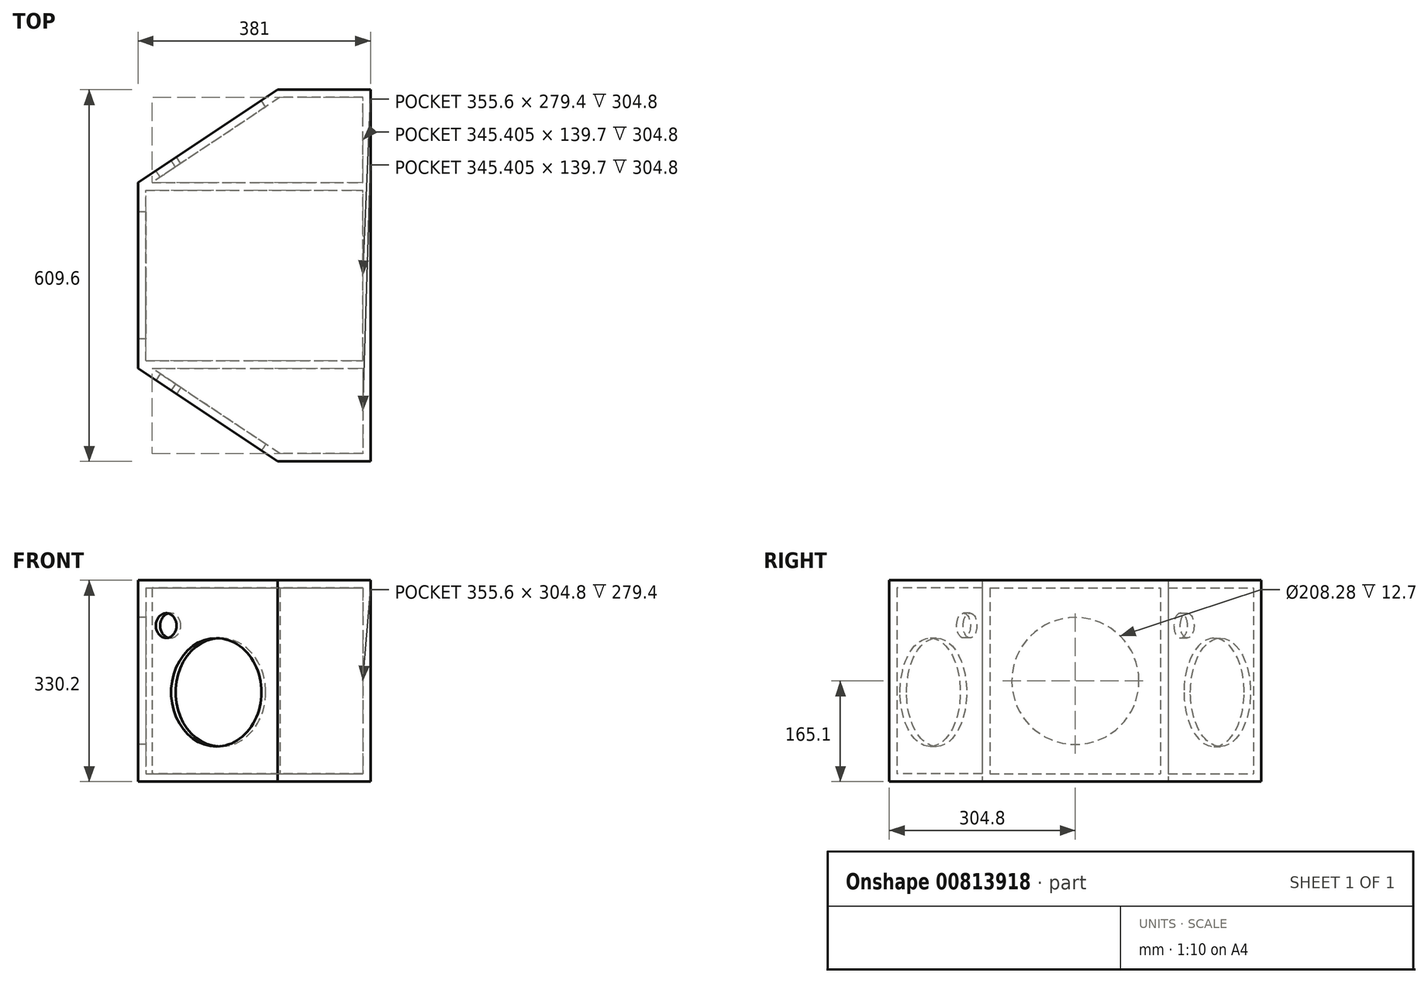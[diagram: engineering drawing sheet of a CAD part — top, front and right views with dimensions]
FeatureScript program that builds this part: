
annotation { "Feature Type Name" : "Feature", "Feature Type Description" : "" }
export const myFeature = defineFeature(function(context is Context, id is Id, definition is map)
    precondition{}
    {
        {
            var Q0;
            Q0=qCreatedBy(makeId("Top.planeOp"),FACE);
            var sketch = newSketch(context, id + "F0", { "sketchPlane" : qUnion([Q0])});
            skLineSegment(sketch, "E0.bottom", {"start": v(0, 0) * mm, "end": v(381, 0) * mm});
            skLineSegment(sketch, "E0.top", {"start": v(0, 304.8) * mm, "end": v(381, 304.8) * mm});
            skLineSegment(sketch, "E0.left", {"start": v(0, 0) * mm, "end": v(0, 304.8) * mm});
            skLineSegment(sketch, "E0.right", {"start": v(381, 0) * mm, "end": v(381, 304.8) * mm});
            skLineSegment(sketch, "E1.0", {"start": v(12.7, 292.1) * mm, "end": v(368.3, 292.1) * mm});
            skLineSegment(sketch, "E1.1", {"start": v(12.7, 12.7) * mm, "end": v(12.7, 292.1) * mm});
            skLineSegment(sketch, "E1.2", {"start": v(12.7, 12.7) * mm, "end": v(368.3, 12.7) * mm});
            skLineSegment(sketch, "E1.3", {"start": v(368.3, 12.7) * mm, "end": v(368.3, 292.1) * mm});
            skPoint(sketch, "E2.2.start.orphan", {"position": v(368.3, 304.8) * mm});
            skPoint(sketch, "E2.0.start.orphan", {"position": v(12.7, 304.8) * mm});
            skPoint(sketch, "E3.1.start.orphan", {"position": v(12.7, 0) * mm});
            skPoint(sketch, "E3.3.start.orphan", {"position": v(368.3, 0) * mm});
            skLineSegment(sketch, "E4", {"start": v(381, 0) * mm, "end": v(381, -152.4) * mm});
            skLineSegment(sketch, "E5", {"start": v(381, -152.4) * mm, "end": v(228.6, -152.4) * mm});
            skLineSegment(sketch, "E6", {"start": v(228.6, -152.4) * mm, "end": v(0, 0) * mm});
            skLineSegment(sketch, "E7.0", {"start": v(232.45, -139.7) * mm, "end": v(22.9, 0) * mm});
            skLineSegment(sketch, "E7.1", {"start": v(368.3, -139.7) * mm, "end": v(232.45, -139.7) * mm});
            skLineSegment(sketch, "E7.2", {"start": v(368.3, 0) * mm, "end": v(368.3, -139.7) * mm});
            skLineSegment(sketch, "E8", {"start": v(381, 304.8) * mm, "end": v(381, 457.2) * mm});
            skLineSegment(sketch, "E9", {"start": v(381, 457.2) * mm, "end": v(228.6, 457.2) * mm});
            skLineSegment(sketch, "E10", {"start": v(228.6, 457.2) * mm, "end": v(0, 304.8) * mm});
            skLineSegment(sketch, "E11.0", {"start": v(232.45, 444.5) * mm, "end": v(22.9, 304.8) * mm});
            skLineSegment(sketch, "E11.1", {"start": v(368.3, 444.5) * mm, "end": v(232.45, 444.5) * mm});
            skLineSegment(sketch, "E11.2", {"start": v(368.3, 304.8) * mm, "end": v(368.3, 444.5) * mm});
            skSolve(sketch);
        }
        {
            var Q0;
            Q0 = qSketchRegion(id + "F0", true);
            extrude(context, id + "F1", {"entities" : qUnion([Q0]), "depth" : 304.8 * mm, "offsetDistance" : 25.4 * mm});
        }
        {
            var Q0;
            Q0=makeQuery(id+"F1.opExtrude","SWEPT_FACE",FACE,{"disambiguationData":[OSD([sQuery(id+"F0.wireOp",EDGE,"E0.left")])]});
            var sketch = newSketch(context, id + "F2", { "sketchPlane" : qUnion([Q0])});
            skLineSegment(sketch, "E12", {"start": v(-152.4, 304.8) * mm, "end": v(-152.4, 0) * mm, "construction": true});
            skCircle(sketch, "E13", {"center": v(-152.4, 152.4) * mm, "radius": 104.14 * mm});
            skSolve(sketch);
        }
        {
            var Q0;
            Q0 = qSketchRegion(id + "F2", true);
            extrude(context, id + "F3", {"entities" : qUnion([Q0]), "operationType" : NewBodyOperationType.REMOVE, "endBound" : BoundingType.UP_TO_NEXT, "oppositeDirection" : true, "depth" : 25.4 * mm, "offsetDistance" : 25.4 * mm});
        }
        {
            var Q0;
            Q0=makeQuery(id+"F1.opExtrude","SWEPT_FACE",FACE,{"disambiguationData":[OSD([sQuery(id+"F0.wireOp",EDGE,"E10")])]});
            var sketch = newSketch(context, id + "F4", { "sketchPlane" : qUnion([Q0])});
            skLineSegment(sketch, "E14", {"start": v(-306.44, 304.8) * mm, "end": v(-306.44, 0) * mm, "construction": true});
            skLineSegment(sketch, "E15", {"start": v(-169.07, 304.8) * mm, "end": v(-443.82, 0) * mm, "construction": true});
            skCircle(sketch, "E16", {"center": v(-323.17, 133.85) * mm, "radius": 88.9 * mm});
            skCircle(sketch, "E17", {"center": v(-224.53, 243.28) * mm, "radius": 20.32 * mm});
            skSolve(sketch);
        }
        {
            var Q0;
            Q0 = qSketchRegion(id + "F4", true);
            extrude(context, id + "F5", {"entities" : qUnion([Q0]), "operationType" : NewBodyOperationType.REMOVE, "endBound" : BoundingType.UP_TO_NEXT, "oppositeDirection" : true, "depth" : 25.4 * mm, "offsetDistance" : 25.4 * mm});
        }
        {
            var Q0;
            Q0=makeQuery(id+"F1.opExtrude","SWEPT_FACE",FACE,{"disambiguationData":[OSD([sQuery(id+"F0.wireOp",EDGE,"E6")])]});
            var sketch = newSketch(context, id + "F6", { "sketchPlane" : qUnion([Q0])});
            skLineSegment(sketch, "E18", {"start": v(0, 304.8) * mm, "end": v(274.74, 0) * mm, "construction": true});
            skCircle(sketch, "E19", {"center": v(154.1, 133.85) * mm, "radius": 88.9 * mm});
            skCircle(sketch, "E20", {"center": v(55.46, 243.28) * mm, "radius": 20.32 * mm});
            skSolve(sketch);
        }
        {
            var Q0;
            Q0 = qSketchRegion(id + "F6", true);
            extrude(context, id + "F7", {"entities" : qUnion([Q0]), "operationType" : NewBodyOperationType.REMOVE, "endBound" : BoundingType.UP_TO_NEXT, "oppositeDirection" : true, "depth" : 25.4 * mm, "offsetDistance" : 25.4 * mm});
        }
        {
            var Q0;
            Q0=makeQuery(id+"F1.opExtrude","CAP_FACE",FACE,{"disambiguationData":[OSD([sQuery(id+"F0.wireOp",EDGE,"E0.left"),sQuery(id+"F0.wireOp",EDGE,"E0.right"),sQuery(id+"F0.wireOp",EDGE,"E0.bottom"),sQuery(id+"F0.wireOp",EDGE,"E0.top"),sQuery(id+"F0.wireOp",EDGE,"E1.0"),sQuery(id+"F0.wireOp",EDGE,"E1.1"),sQuery(id+"F0.wireOp",EDGE,"E1.2"),sQuery(id+"F0.wireOp",EDGE,"E1.3"),sQuery(id+"F0.wireOp",EDGE,"E4"),sQuery(id+"F0.wireOp",EDGE,"E5"),sQuery(id+"F0.wireOp",EDGE,"E6"),sQuery(id+"F0.wireOp",EDGE,"E7.0"),sQuery(id+"F0.wireOp",EDGE,"E7.1"),sQuery(id+"F0.wireOp",EDGE,"E7.2"),sQuery(id+"F0.wireOp",EDGE,"E8"),sQuery(id+"F0.wireOp",EDGE,"E9"),sQuery(id+"F0.wireOp",EDGE,"E10"),sQuery(id+"F0.wireOp",EDGE,"E11.0"),sQuery(id+"F0.wireOp",EDGE,"E11.1"),sQuery(id+"F0.wireOp",EDGE,"E11.2")])],"isStart":true});
            var sketch = newSketch(context, id + "F8", { "sketchPlane" : qUnion([Q0])});
            skLineSegment(sketch, "E21", {"start": v(381, 152.4) * mm, "end": v(381, -457.2) * mm});
            skLineSegment(sketch, "E22", {"start": v(381, -457.2) * mm, "end": v(228.6, -457.2) * mm});
            skLineSegment(sketch, "E23", {"start": v(228.6, -457.2) * mm, "end": v(0, -304.8) * mm});
            skLineSegment(sketch, "E24", {"start": v(0, -304.8) * mm, "end": v(0, 0) * mm});
            skLineSegment(sketch, "E25", {"start": v(0, 0) * mm, "end": v(228.6, 152.4) * mm});
            skLineSegment(sketch, "E26", {"start": v(228.6, 152.4) * mm, "end": v(381, 152.4) * mm});
            skSolve(sketch);
        }
        {
            var Q0;
            Q0 = qSketchRegion(id + "F8", true);
            extrude(context, id + "F9", {"entities" : qUnion([Q0]), "operationType" : NewBodyOperationType.ADD, "depth" : 12.7 * mm, "offsetDistance" : 25.4 * mm});
        }
        {
            var Q0;
            Q0=makeQuery(id+"F1.opExtrude","CAP_FACE",FACE,{"disambiguationData":[OSD([sQuery(id+"F0.wireOp",EDGE,"E0.left"),sQuery(id+"F0.wireOp",EDGE,"E0.right"),sQuery(id+"F0.wireOp",EDGE,"E0.bottom"),sQuery(id+"F0.wireOp",EDGE,"E0.top"),sQuery(id+"F0.wireOp",EDGE,"E1.0"),sQuery(id+"F0.wireOp",EDGE,"E1.1"),sQuery(id+"F0.wireOp",EDGE,"E1.2"),sQuery(id+"F0.wireOp",EDGE,"E1.3"),sQuery(id+"F0.wireOp",EDGE,"E4"),sQuery(id+"F0.wireOp",EDGE,"E5"),sQuery(id+"F0.wireOp",EDGE,"E6"),sQuery(id+"F0.wireOp",EDGE,"E7.0"),sQuery(id+"F0.wireOp",EDGE,"E7.1"),sQuery(id+"F0.wireOp",EDGE,"E7.2"),sQuery(id+"F0.wireOp",EDGE,"E8"),sQuery(id+"F0.wireOp",EDGE,"E9"),sQuery(id+"F0.wireOp",EDGE,"E10"),sQuery(id+"F0.wireOp",EDGE,"E11.0"),sQuery(id+"F0.wireOp",EDGE,"E11.1"),sQuery(id+"F0.wireOp",EDGE,"E11.2")])],"isStart":false});
            var sketch = newSketch(context, id + "F10", { "sketchPlane" : qUnion([Q0])});
            skLineSegment(sketch, "E27", {"start": v(381, 457.2) * mm, "end": v(381, -152.4) * mm});
            skLineSegment(sketch, "E28", {"start": v(381, -152.4) * mm, "end": v(228.6, -152.4) * mm});
            skLineSegment(sketch, "E29", {"start": v(228.6, -152.4) * mm, "end": v(0, 0) * mm});
            skLineSegment(sketch, "E30", {"start": v(0, 0) * mm, "end": v(0, 304.8) * mm});
            skLineSegment(sketch, "E31", {"start": v(0, 304.8) * mm, "end": v(228.6, 457.2) * mm});
            skLineSegment(sketch, "E32", {"start": v(228.6, 457.2) * mm, "end": v(381, 457.2) * mm});
            skSolve(sketch);
        }
        {
            var Q0;
            Q0 = qSketchRegion(id + "F10", true);
            extrude(context, id + "F11", {"entities" : qUnion([Q0]), "operationType" : NewBodyOperationType.ADD, "depth" : 12.7 * mm, "offsetDistance" : 25.4 * mm});
        }
    });
